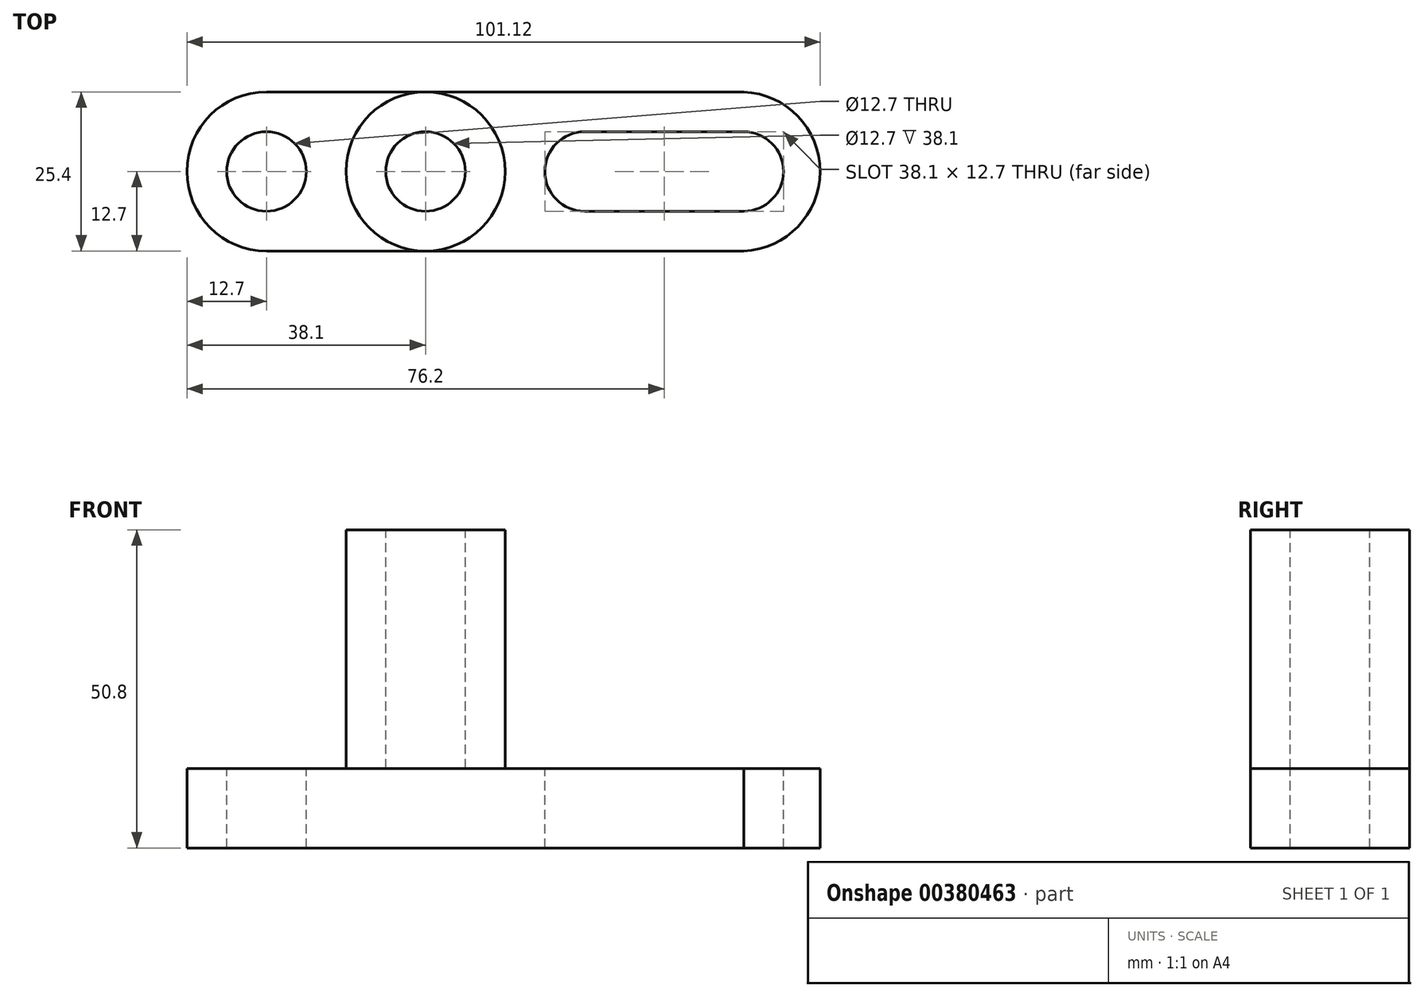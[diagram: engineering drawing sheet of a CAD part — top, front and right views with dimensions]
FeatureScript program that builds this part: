
annotation { "Feature Type Name" : "Feature", "Feature Type Description" : "" }
export const myFeature = defineFeature(function(context is Context, id is Id, definition is map)
    precondition{}
    {
        {
            var Q0;
            Q0=qCreatedBy(makeId("Front.planeOp"),FACE);
            var sketch = newSketch(context, id + "F0", { "sketchPlane" : qUnion([Q0])});
            skLineSegment(sketch, "E0", {"start": v(0, 0) * mm, "end": v(101.6, 0) * mm});
            skLineSegment(sketch, "E1", {"start": v(101.6, 0) * mm, "end": v(101.6, 12.7) * mm});
            skLineSegment(sketch, "E2", {"start": v(101.6, 12.7) * mm, "end": v(0, 12.7) * mm});
            skLineSegment(sketch, "E3", {"start": v(0, 12.7) * mm, "end": v(0, 0) * mm});
            skSolve(sketch);
        }
        {
            var Q0;
            Q0 = qSketchRegion(id + "F0", true);
            extrude(context, id + "F1", {"entities" : qUnion([Q0]), "depth" : 25.4 * mm});
        }
        {
            var Q0;
            Q0=makeQuery(id+"F1.opExtrude","SWEPT_FACE",FACE,{"disambiguationData":[OSD([sQuery(id+"F0.wireOp",EDGE,"E2")])]});
            var sketch = newSketch(context, id + "F2", { "sketchPlane" : qUnion([Q0])});
            skCircle(sketch, "E4", {"center": v(12.7, -12.7) * mm, "radius": 6.35 * mm});
            skSolve(sketch);
        }
        {
            var Q0;
            Q0=makeQuery(id+"F2.imprint","IMPRINT",FACE,{"disambiguationData":[TD([[makeQuery(id+"F2.imprint","IMPRINT",EDGE,{"derivedFrom":sQuery(id+"F2.wireOp",EDGE,"E4")}),1.0]])]});
            extrude(context, id + "F3", {"entities" : qUnion([Q0]), "operationType" : NewBodyOperationType.REMOVE, "oppositeDirection" : true, "depth" : 25.4 * mm});
        }
        {
            var Q0;
            Q0=makeQuery(id+"F1.opExtrude","SWEPT_FACE",FACE,{"disambiguationData":[OSD([sQuery(id+"F0.wireOp",EDGE,"E2")])]});
            var sketch = newSketch(context, id + "F4", { "sketchPlane" : qUnion([Q0])});
            skArc(sketch, "E5", {"start": v(12.7, 0) * mm, "mid": v(0, -12.7) * mm, "end": v(12.7, -25.4) * mm});
            skSolve(sketch);
        }
        {
            var Q0;
            {var subQ0=sQuery(id+"F4.wireOp",EDGE,"E5");var subQ1=sQuery(id+"F0.wireOp",EDGE,"E2");var subQ2=makeQuery(id+"F1.opExtrude","CAP_EDGE",EDGE,{"disambiguationData":[OSD([subQ1])],"isStart":true});var subQ3=makeQuery(id+"F4.imprint","INTERSECT",VERTEX,{"derivedFrom":[subQ2,subQ0]});Q0=makeQuery(id+"F4.imprint","IMPRINT",FACE,{"disambiguationData":[TD([[makeQuery(id+"F4.imprint","IMPRINT",EDGE,{"disambiguationData":[TD([[subQ3,-1.0]])],"derivedFrom":subQ0}),-1.0]])]});}
            var Q1;
            {var subQ0=sQuery(id+"F4.wireOp",EDGE,"E5");var subQ1=sQuery(id+"F0.wireOp",EDGE,"E2");var subQ2=makeQuery(id+"F1.opExtrude","CAP_EDGE",EDGE,{"disambiguationData":[OSD([subQ1])],"isStart":false});var subQ3=makeQuery(id+"F4.imprint","INTERSECT",VERTEX,{"derivedFrom":[subQ2,subQ0]});Q1=makeQuery(id+"F4.imprint","IMPRINT",FACE,{"disambiguationData":[TD([[makeQuery(id+"F4.imprint","IMPRINT",EDGE,{"disambiguationData":[TD([[subQ3,1.0]])],"derivedFrom":subQ0}),-1.0]])]});}
            extrude(context, id + "F5", {"entities" : qUnion([Q0, Q1]), "operationType" : NewBodyOperationType.REMOVE, "oppositeDirection" : true, "depth" : 25.4 * mm});
        }
        {
            var Q0;
            Q0=makeQuery(id+"F1.opExtrude","SWEPT_FACE",FACE,{"disambiguationData":[OSD([sQuery(id+"F0.wireOp",EDGE,"E2")])]});
            var sketch = newSketch(context, id + "F6", { "sketchPlane" : qUnion([Q0])});
            skCircle(sketch, "E6", {"center": v(63.5, -12.7) * mm, "radius": 6.35 * mm});
            skCircle(sketch, "E7", {"center": v(88.9, -12.7) * mm, "radius": 6.35 * mm});
            skLineSegment(sketch, "E8", {"start": v(63.5, -6.35) * mm, "end": v(88.9, -6.35) * mm});
            skLineSegment(sketch, "E9", {"start": v(63.5, -19.05) * mm, "end": v(88.9, -19.05) * mm});
            skSolve(sketch);
        }
        {
            var Q0;
            {var subQ0=sQuery(id+"F6.wireOp",EDGE,"E8");Q0=makeQuery(id+"F6.imprint","IMPRINT",FACE,{"disambiguationData":[TD([[makeQuery(id+"F6.imprint","IMPRINT",EDGE,{"derivedFrom":subQ0}),-1.0]])]});}
            var Q1;
            {var subQ0=sQuery(id+"F6.wireOp",EDGE,"E6");var subQ1=makeQuery(id+"F6.imprint","INTERSECT",VERTEX,{"derivedFrom":[subQ0,sQuery(id+"F6.wireOp",EDGE,"E8")]});Q1=makeQuery(id+"F6.imprint","IMPRINT",FACE,{"disambiguationData":[TD([[makeQuery(id+"F6.imprint","IMPRINT",EDGE,{"disambiguationData":[TD([[subQ1,-1.0]])],"derivedFrom":subQ0}),1.0]])]});}
            var Q2;
            {var subQ0=sQuery(id+"F6.wireOp",EDGE,"E7");var subQ1=makeQuery(id+"F6.imprint","INTERSECT",VERTEX,{"derivedFrom":[subQ0,sQuery(id+"F6.wireOp",EDGE,"E8")]});Q2=makeQuery(id+"F6.imprint","IMPRINT",FACE,{"disambiguationData":[TD([[makeQuery(id+"F6.imprint","IMPRINT",EDGE,{"disambiguationData":[TD([[subQ1,-1.0]])],"derivedFrom":subQ0}),1.0]])]});}
            extrude(context, id + "F7", {"entities" : qUnion([Q0, Q1, Q2]), "operationType" : NewBodyOperationType.REMOVE, "oppositeDirection" : true, "depth" : 25.4 * mm});
        }
        {
            var Q0;
            Q0=makeQuery(id+"F1.opExtrude","SWEPT_FACE",FACE,{"disambiguationData":[OSD([sQuery(id+"F0.wireOp",EDGE,"E2")])]});
            var sketch = newSketch(context, id + "F8", { "sketchPlane" : qUnion([Q0])});
            skCircle(sketch, "E10", {"center": v(38.1, -12.7) * mm, "radius": 12.7 * mm});
            skPoint(sketch, "E10.centerSnap0", {"position": v(0, -12.7) * mm});
            skSolve(sketch);
        }
        {
            var Q0;
            {var subQ0=sQuery(id+"F8.wireOp",EDGE,"E10");var subQ1=sQuery(id+"F0.wireOp",EDGE,"E2");var subQ2=makeQuery(id+"F8.imprint","INTERSECT",VERTEX,{"derivedFrom":[makeQuery(id+"F1.opExtrude","CAP_EDGE",EDGE,{"disambiguationData":[OSD([subQ1])],"isStart":true}),subQ0]});Q0=makeQuery(id+"F8.imprint","IMPRINT",FACE,{"disambiguationData":[TD([[makeQuery(id+"F8.imprint","IMPRINT",EDGE,{"disambiguationData":[TD([[subQ2,-1.0]])],"derivedFrom":subQ0}),1.0]])]});}
            extrude(context, id + "F9", {"entities" : qUnion([Q0]), "operationType" : NewBodyOperationType.ADD, "depth" : 38.1 * mm});
        }
        {
            var Q0;
            Q0=makeQuery(id+"F9.opExtrude","CAP_FACE",FACE,{"disambiguationData":[OSD([sQuery(id+"F8.wireOp",EDGE,"E10")])],"isStart":false});
            var sketch = newSketch(context, id + "F10", { "sketchPlane" : qUnion([Q0])});
            skCircle(sketch, "E11", {"center": v(38.1, -12.7) * mm, "radius": 6.35 * mm});
            skSolve(sketch);
        }
        {
            var Q0;
            Q0=makeQuery(id+"F10.imprint","IMPRINT",FACE,{"disambiguationData":[TD([[makeQuery(id+"F10.imprint","IMPRINT",EDGE,{"derivedFrom":sQuery(id+"F10.wireOp",EDGE,"E11")}),1.0]])]});
            extrude(context, id + "F11", {"entities" : qUnion([Q0]), "operationType" : NewBodyOperationType.REMOVE, "oppositeDirection" : true, "depth" : 38.1 * mm});
        }
        {
            var Q0;
            {var subQ0=sQuery(id+"F0.wireOp",EDGE,"E2");var subQ1=makeQuery(id+"F1.opExtrude","SWEPT_FACE",FACE,{"disambiguationData":[OSD([subQ0])]});var subQ2=sQuery(id+"F0.wireOp",EDGE,"E1");Q0=makeQuery(id+"F9.boolean.opBoolean","SPLIT",FACE,{"disambiguationData":[TD([makeQuery(id+"F1.opExtrude","SWEPT_FACE",FACE,{"disambiguationData":[OSD([subQ2])]})])],"derivedFrom":subQ1});}
            var sketch = newSketch(context, id + "F12", { "sketchPlane" : qUnion([Q0])});
            skArc(sketch, "E12", {"start": v(88.9, -25.4) * mm, "mid": v(101.12, -12.7) * mm, "end": v(88.9, 0) * mm});
            skSolve(sketch);
        }
        {
            var Q0;
            {var subQ0=sQuery(id+"F12.wireOp",EDGE,"E12");Q0=makeQuery(id+"F12.imprint","IMPRINT",FACE,{"disambiguationData":[TD([[makeQuery(id+"F12.imprint","IMPRINT",EDGE,{"derivedFrom":subQ0}),-1.0]])]});}
            extrude(context, id + "F13", {"entities" : qUnion([Q0]), "operationType" : NewBodyOperationType.REMOVE, "oppositeDirection" : true, "depth" : 25.4 * mm});
        }
    });
